# Revit family: VRS-3492
name_source: partatom
category: Lighting Fixtures
units: mm (PartAtom-declared; Revit-internal decimal feet)

## family parameters
Always vertical = Yes
Cut with Voids When Loaded = No
Host = Ceiling
Light Source = Yes
OmniClass Number = 23.80.70.11
OmniClass Title = Luminaries for Internal Lighting
Part Type = Normal
Room Calculation Point = No
Round Connector Dimension = Use Diameter
Shared = No

## types (4) — shared parameters
Assembly Code = D5020200
Color Filter = 16777215
Description = LED Vandal Resistant Surface Mount
Dimming Lamp Color Temperature Shift = <None>
Emit Shape Visible in Rendering = No
Emit from Rectangle Length = 1' - 1"
Emit from Rectangle Width = 4' - 1 5/8"
Housing Finish = Metal - Viscor - White
Lamp = LED
Length = 4' - 1 5/8"
Lens Finish = Acrylic - Viscor - Frosted Prismatic P12
Manufacturer = CERTOLUX by VISCOR
Model = VRS-3492
Tilt Angle = 90.00°
URL = https://www.viscor.com
Voltage = 0 V
Width = 1' - 1"

## per-type parameters (varying)
| type | Apparent Load | Lamp Wattage | Photometric Web File |
| VRS-3492-1X4-LED840K39L-P13 | 32 VA | 32 VA |  |
| VRS-3492-1X4-LED840K26L-P13 | 22 VA | 22 VA | VRS-3492-1X4-LED840K26LUNV-P13.ies |
| VRS-3492-1X4-LED840K52L-P13 | 42 VA | 42 VA | VRS-3492-1X4-LED840K52LUNV-P13.ies |
| VRS-3492-1X4-LED840K78L-P13 | 70 VA | 70 VA | VRS-3492-1X4-LED-840K78LUNV-P13.ies |

## geometry (parser evidence)
native form markers: Sweep x1
no freeform markers — native parametric forms only
